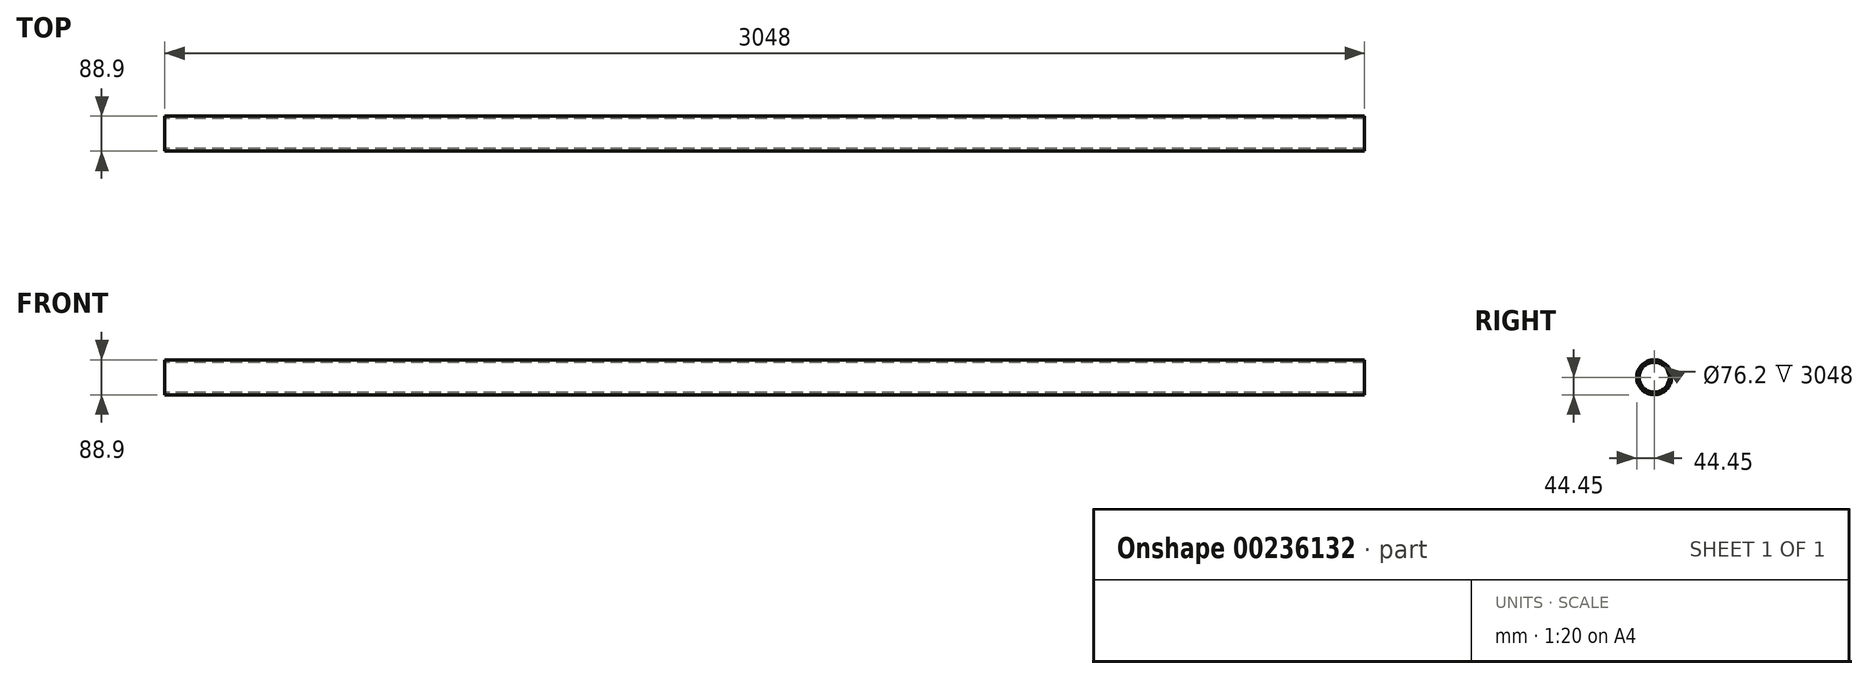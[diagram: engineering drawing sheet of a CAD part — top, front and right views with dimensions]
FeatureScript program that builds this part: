
annotation { "Feature Type Name" : "Feature", "Feature Type Description" : "" }
export const myFeature = defineFeature(function(context is Context, id is Id, definition is map)
    precondition{}
    {
        {
            var Q0;
            Q0=qCreatedBy(makeId("Right.planeOp"),FACE);
            var sketch = newSketch(context, id + "F0", { "sketchPlane" : qUnion([Q0])});
            skCircle(sketch, "E0", {"center": v(0, 0) * mm, "radius": 44.45 * mm});
            skCircle(sketch, "E1", {"center": v(0, 0) * mm, "radius": 38.1 * mm});
            skSolve(sketch);
        }
        {
            var Q0;
            Q0 = qSketchRegion(id + "F0", true);
            extrude(context, id + "F1", {"entities" : qUnion([Q0]), "endBound" : BoundingType.SYMMETRIC, "depth" : 3048 * mm});
        }
    });
